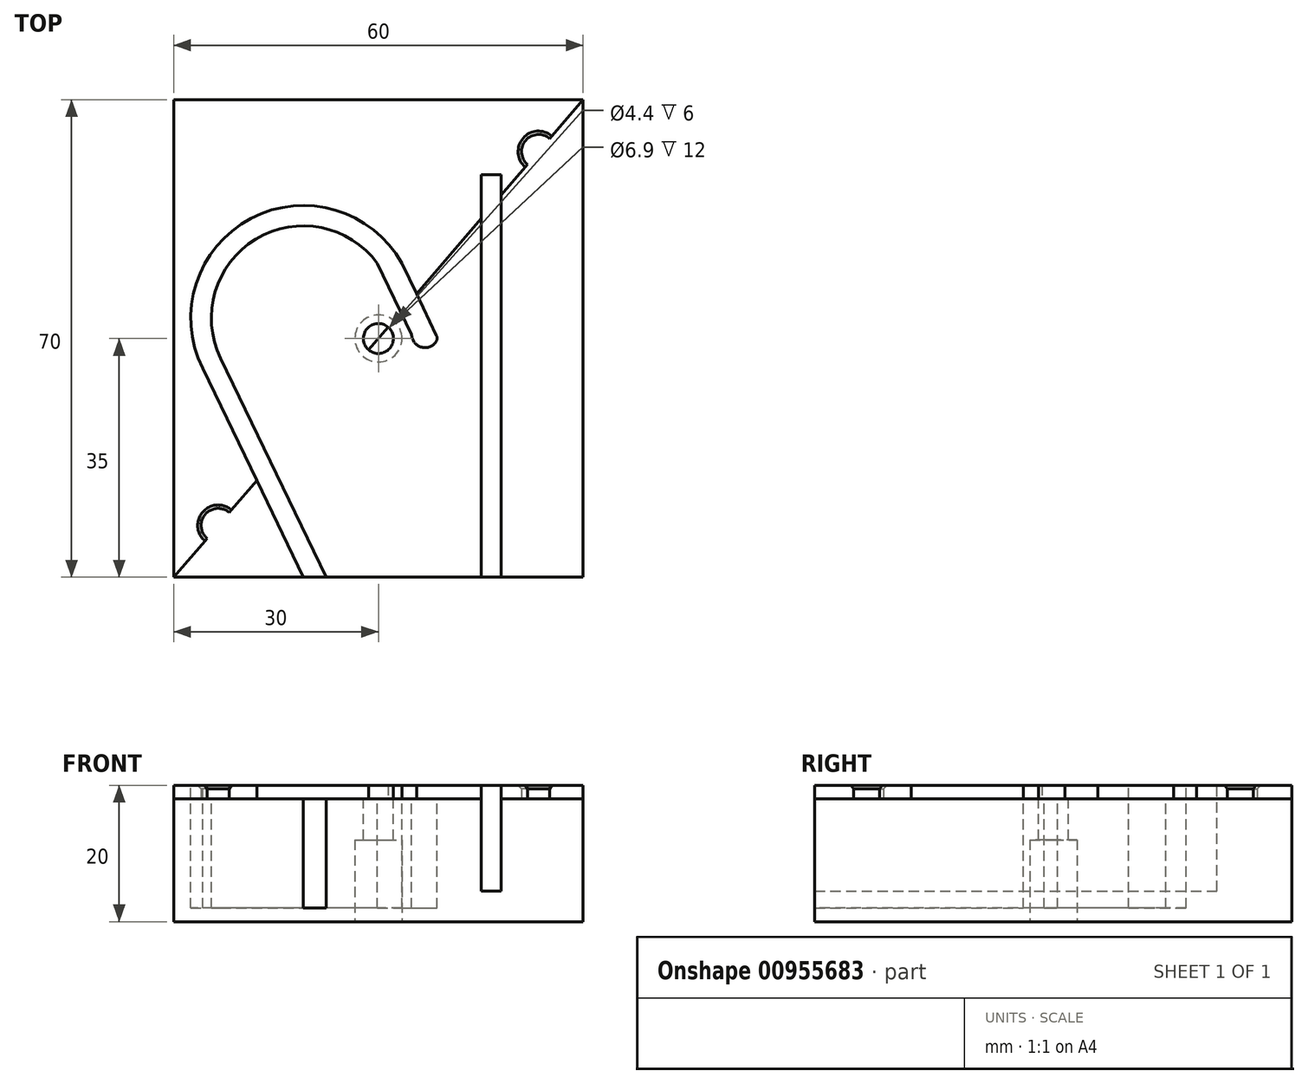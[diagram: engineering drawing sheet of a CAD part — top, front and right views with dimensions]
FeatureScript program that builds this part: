
annotation { "Feature Type Name" : "Feature", "Feature Type Description" : "" }
export const myFeature = defineFeature(function(context is Context, id is Id, definition is map)
    precondition{}
    {
        {
            var Q0;
            Q0=qCreatedBy(makeId("Top.planeOp"),FACE);
            var sketch = newSketch(context, id + "F0", { "sketchPlane" : qUnion([Q0])});
            skLineSegment(sketch, "E0.bottom", {"start": v(0, 0) * mm, "end": v(60, 0) * mm});
            skLineSegment(sketch, "E0.top", {"start": v(0, -70) * mm, "end": v(60, -70) * mm});
            skLineSegment(sketch, "E0.left", {"start": v(0, 0) * mm, "end": v(0, -70) * mm});
            skLineSegment(sketch, "E0.right", {"start": v(60, 0) * mm, "end": v(60, -70) * mm});
            skSolve(sketch);
        }
        {
            var Q0;
            Q0=makeQuery(id+"F0.imprint","IMPRINT",FACE,{"disambiguationData":[TD([[makeQuery(id+"F0.imprint","IMPRINT",EDGE,{"derivedFrom":sQuery(id+"F0.wireOp",EDGE,"E0.bottom")}),-1.0]])]});
            extrude(context, id + "F1", {"entities" : qUnion([Q0]), "depth" : 18 * mm, "offsetDistance" : 25 * mm});
        }
        {
            var Q0;
            Q0=makeQuery(id+"F1.opExtrude","CAP_FACE",FACE,{"disambiguationData":[OSD([sQuery(id+"F0.wireOp",EDGE,"E0.bottom"),sQuery(id+"F0.wireOp",EDGE,"E0.top"),sQuery(id+"F0.wireOp",EDGE,"E0.left"),sQuery(id+"F0.wireOp",EDGE,"E0.right")])],"isStart":false});
            var sketch = newSketch(context, id + "F2", { "sketchPlane" : qUnion([Q0])});
            skLineSegment(sketch, "E1", {"start": v(60, -70) * mm, "end": v(48, -70) * mm});
            skLineSegment(sketch, "E2.bottom", {"start": v(48, -70) * mm, "end": v(45.1, -70) * mm});
            skLineSegment(sketch, "E2.top", {"start": v(48, -11) * mm, "end": v(45.1, -11) * mm});
            skLineSegment(sketch, "E2.left", {"start": v(48, -70) * mm, "end": v(48, -11) * mm});
            skLineSegment(sketch, "E2.right", {"start": v(45.1, -70) * mm, "end": v(45.1, -11) * mm});
            skSolve(sketch);
        }
        {
            var Q0;
            Q0=makeQuery(id+"F2.imprint","IMPRINT",FACE,{"disambiguationData":[TD([[makeQuery(id+"F2.imprint","IMPRINT",EDGE,{"derivedFrom":sQuery(id+"F2.wireOp",EDGE,"E2.bottom")}),1.0]])]});
            extrude(context, id + "F3", {"entities" : qUnion([Q0]), "operationType" : NewBodyOperationType.REMOVE, "oppositeDirection" : true, "depth" : 13.5 * mm, "offsetDistance" : 25 * mm});
        }
        {
            var Q0;
            Q0=makeQuery(id+"F1.opExtrude","CAP_FACE",FACE,{"disambiguationData":[OSD([sQuery(id+"F0.wireOp",EDGE,"E0.bottom"),sQuery(id+"F0.wireOp",EDGE,"E0.top"),sQuery(id+"F0.wireOp",EDGE,"E0.left"),sQuery(id+"F0.wireOp",EDGE,"E0.right")])],"isStart":false});
            var sketch = newSketch(context, id + "F4", { "sketchPlane" : qUnion([Q0])});
            skLineSegment(sketch, "E3", {"start": v(0, -70) * mm, "end": v(19, -70) * mm});
            skLineSegment(sketch, "E4", {"start": v(19, -70) * mm, "end": v(4.24, -39.37) * mm});
            skLineSegment(sketch, "E5", {"start": v(33.43, -24) * mm, "end": v(38.5, -34.54) * mm});
            skArc(sketch, "E6", {"start": v(29.87, -24) * mm, "mid": v(12.02, -20.44) * mm, "end": v(6.85, -37.89) * mm});
            skLineSegment(sketch, "E7", {"start": v(29.87, -24) * mm, "end": v(34.88, -34.4) * mm});
            skLineSegment(sketch, "E8", {"start": v(6.85, -37.89) * mm, "end": v(22.33, -70) * mm});
            skArc(sketch, "E9.trimOffspring", {"start": v(33.43, -24) * mm, "mid": v(11.3, -17.4) * mm, "end": v(4.24, -39.37) * mm});
            skLineSegment(sketch, "E10", {"start": v(19, -70) * mm, "end": v(22.33, -70) * mm});
            skArc(sketch, "E11", {"start": v(34.88, -34.4) * mm, "mid": v(36.22, -36.25) * mm, "end": v(38.4, -35.58) * mm});
            skPoint(sketch, "E12.visualSharp", {"position": v(38.72, -34.97) * mm});
            skArc(sketch, "E12.filletArc", {"start": v(38.4, -35.58) * mm, "mid": v(38.6, -35.07) * mm, "end": v(38.5, -34.54) * mm});
            skSolve(sketch);
        }
        {
            var Q0;
            Q0=makeQuery(id+"F4.imprint","IMPRINT",FACE,{"disambiguationData":[TD([[makeQuery(id+"F4.imprint","IMPRINT",EDGE,{"derivedFrom":sQuery(id+"F4.wireOp",EDGE,"E4")}),-1.0]])]});
            extrude(context, id + "F5", {"entities" : qUnion([Q0]), "operationType" : NewBodyOperationType.REMOVE, "oppositeDirection" : true, "depth" : 16 * mm, "offsetDistance" : 25 * mm});
        }
        {
            var Q0;
            Q0=makeQuery(id+"F1.opExtrude","CAP_FACE",FACE,{"disambiguationData":[OSD([sQuery(id+"F0.wireOp",EDGE,"E0.bottom"),sQuery(id+"F0.wireOp",EDGE,"E0.top"),sQuery(id+"F0.wireOp",EDGE,"E0.left"),sQuery(id+"F0.wireOp",EDGE,"E0.right")])],"isStart":false});
            var sketch = newSketch(context, id + "F6", { "sketchPlane" : qUnion([Q0])});
            skLineSegment(sketch, "E13", {"start": v(0, -70) * mm, "end": v(28.57, -36.67) * mm});
            skLineSegment(sketch, "E14", {"start": v(0, 0) * mm, "end": v(28.57, -33.33) * mm});
            skCircle(sketch, "E15", {"center": v(30, -35) * mm, "radius": 2.2 * mm});
            skLineSegment(sketch, "E16.trimOffspring", {"start": v(31.43, -33.33) * mm, "end": v(60, 0) * mm});
            skLineSegment(sketch, "E17.trimOffspring", {"start": v(31.43, -36.67) * mm, "end": v(60, -70) * mm});
            skSolve(sketch);
        }
        {
            var Q0;
            {var subQ0=sQuery(id+"F6.wireOp",EDGE,"E15");var subQ1=makeQuery(id+"F6.imprint","INTERSECT",VERTEX,{"derivedFrom":[sQuery(id+"F6.wireOp",EDGE,"E14"),subQ0]});Q0=makeQuery(id+"F6.imprint","IMPRINT",FACE,{"disambiguationData":[TD([[makeQuery(id+"F6.imprint","IMPRINT",EDGE,{"disambiguationData":[TD([[subQ1,1.0]])],"derivedFrom":subQ0}),1.0]])]});}
            extrude(context, id + "F7", {"entities" : qUnion([Q0]), "operationType" : NewBodyOperationType.REMOVE, "oppositeDirection" : true, "depth" : 25 * mm, "offsetDistance" : 25 * mm});
        }
        {
            var Q0;
            Q0=makeQuery(id+"F1.opExtrude","CAP_FACE",FACE,{"disambiguationData":[OSD([sQuery(id+"F0.wireOp",EDGE,"E0.bottom"),sQuery(id+"F0.wireOp",EDGE,"E0.top"),sQuery(id+"F0.wireOp",EDGE,"E0.left"),sQuery(id+"F0.wireOp",EDGE,"E0.right")])],"isStart":false});
            var sketch = newSketch(context, id + "F8", { "sketchPlane" : qUnion([Q0])});
            skLineSegment(sketch, "E18", {"start": v(0, -70) * mm, "end": v(60, 0) * mm});
            skLineSegment(sketch, "E19", {"start": v(60, 0) * mm, "end": v(53.5, -7.6) * mm});
            skLineSegment(sketch, "E20", {"start": v(0, -70) * mm, "end": v(6.5, -62.4) * mm});
            skCircle(sketch, "E21", {"center": v(6.5, -62.4) * mm, "radius": 2.5 * mm});
            skCircle(sketch, "E22", {"center": v(53.5, -7.6) * mm, "radius": 2.5 * mm});
            skSolve(sketch);
        }
        {
            var Q0;
            {var subQ0=sQuery(id+"F8.wireOp",EDGE,"E20");var subQ1=sQuery(id+"F8.wireOp",EDGE,"E18");var subQ2=makeQuery(id+"F8.imprint","INTERSECT",VERTEX,{"derivedFrom":[subQ1,subQ0]});Q0=makeQuery(id+"F8.imprint","IMPRINT",FACE,{"disambiguationData":[TD([[makeQuery(id+"F8.imprint","IMPRINT",EDGE,{"disambiguationData":[TD([[subQ2,-1.0]])],"derivedFrom":subQ1}),1.0]])]});}
            var Q1;
            {var subQ0=sQuery(id+"F8.wireOp",EDGE,"E19");var subQ1=sQuery(id+"F8.wireOp",EDGE,"E18");var subQ2=makeQuery(id+"F8.imprint","INTERSECT",VERTEX,{"derivedFrom":[subQ1,subQ0]});Q1=makeQuery(id+"F8.imprint","IMPRINT",FACE,{"disambiguationData":[TD([[makeQuery(id+"F8.imprint","IMPRINT",EDGE,{"disambiguationData":[TD([[subQ2,1.0]])],"derivedFrom":subQ1}),-1.0]])]});}
            var Q2;
            {var subQ0=sQuery(id+"F8.wireOp",EDGE,"E20");var subQ1=sQuery(id+"F8.wireOp",EDGE,"E18");var subQ2=makeQuery(id+"F8.imprint","INTERSECT",VERTEX,{"derivedFrom":[subQ1,subQ0]});Q2=makeQuery(id+"F8.imprint","IMPRINT",FACE,{"disambiguationData":[TD([[makeQuery(id+"F8.imprint","IMPRINT",EDGE,{"disambiguationData":[TD([[subQ2,-1.0]])],"derivedFrom":subQ1}),-1.0]])]});}
            var Q3;
            {var subQ0=sQuery(id+"F8.wireOp",EDGE,"E19");var subQ1=sQuery(id+"F8.wireOp",EDGE,"E18");var subQ2=makeQuery(id+"F8.imprint","INTERSECT",VERTEX,{"derivedFrom":[subQ1,subQ0]});Q3=makeQuery(id+"F8.imprint","IMPRINT",FACE,{"disambiguationData":[TD([[makeQuery(id+"F8.imprint","IMPRINT",EDGE,{"disambiguationData":[TD([[subQ2,1.0]])],"derivedFrom":subQ1}),1.0]])]});}
            extrude(context, id + "F9", {"entities" : qUnion([Q0, Q1, Q2, Q3]), "operationType" : NewBodyOperationType.ADD, "depth" : 2 * mm, "offsetDistance" : 25 * mm});
        }
        {
            var Q0;
            Q0=makeQuery(id+"F9.opExtrude","CAP_EDGE",EDGE,{"disambiguationData":[OSD([sQuery(id+"F8.wireOp",EDGE,"E21")])],"isStart":false});
            var Q1;
            Q1=makeQuery(id+"F9.opExtrude","CAP_EDGE",EDGE,{"disambiguationData":[OSD([sQuery(id+"F8.wireOp",EDGE,"E22")])],"isStart":false});
            var Q2;
            Q2=makeQuery(id+"F7.boolean.opBoolean","COPY",EDGE,{"derivedFrom":makeQuery(id+"F7.opExtrude","CAP_EDGE",EDGE,{"disambiguationData":[OSD([sQuery(id+"F6.wireOp",EDGE,"E15")])],"isStart":true})});
            chamfer(context, id + "F10", {"entities" : qUnion([Q0, Q1, Q2]), "width" : 0.5 * mm, "tangentPropagation" : true});
        }
        {
            var Q0;
            Q0=makeQuery(id+"F1.opExtrude","CAP_FACE",FACE,{"disambiguationData":[OSD([sQuery(id+"F0.wireOp",EDGE,"E0.bottom"),sQuery(id+"F0.wireOp",EDGE,"E0.top"),sQuery(id+"F0.wireOp",EDGE,"E0.left"),sQuery(id+"F0.wireOp",EDGE,"E0.right")])],"isStart":true});
            var sketch = newSketch(context, id + "F11", { "sketchPlane" : qUnion([Q0])});
            skCircle(sketch, "E23", {"center": v(30, 35) * mm, "radius": 3.45 * mm});
            skSolve(sketch);
        }
        {
            var Q0;
            Q0=makeQuery(id+"F11.imprint","IMPRINT",FACE,{"disambiguationData":[TD([[makeQuery(id+"F11.imprint","IMPRINT",EDGE,{"derivedFrom":makeQuery(id+"F7.boolean.opBoolean","INTERSECT",EDGE,{"derivedFrom":[makeQuery(id+"F1.opExtrude","CAP_FACE",FACE,{"disambiguationData":[OSD([sQuery(id+"F0.wireOp",EDGE,"E0.bottom"),sQuery(id+"F0.wireOp",EDGE,"E0.top"),sQuery(id+"F0.wireOp",EDGE,"E0.left"),sQuery(id+"F0.wireOp",EDGE,"E0.right")])],"isStart":true}),makeQuery(id+"F7.opExtrude","SWEPT_FACE",FACE,{"disambiguationData":[OSD([sQuery(id+"F6.wireOp",EDGE,"E15")])]})]})}),-1.0]])]});
            var Q1;
            Q1=makeQuery(id+"F11.imprint","IMPRINT",FACE,{"disambiguationData":[TD([[makeQuery(id+"F11.imprint","IMPRINT",EDGE,{"derivedFrom":sQuery(id+"F11.wireOp",EDGE,"E23")}),1.0]])]});
            extrude(context, id + "F12", {"entities" : qUnion([Q0, Q1]), "operationType" : NewBodyOperationType.REMOVE, "oppositeDirection" : true, "depth" : 12 * mm, "offsetDistance" : 25 * mm});
        }
    });
